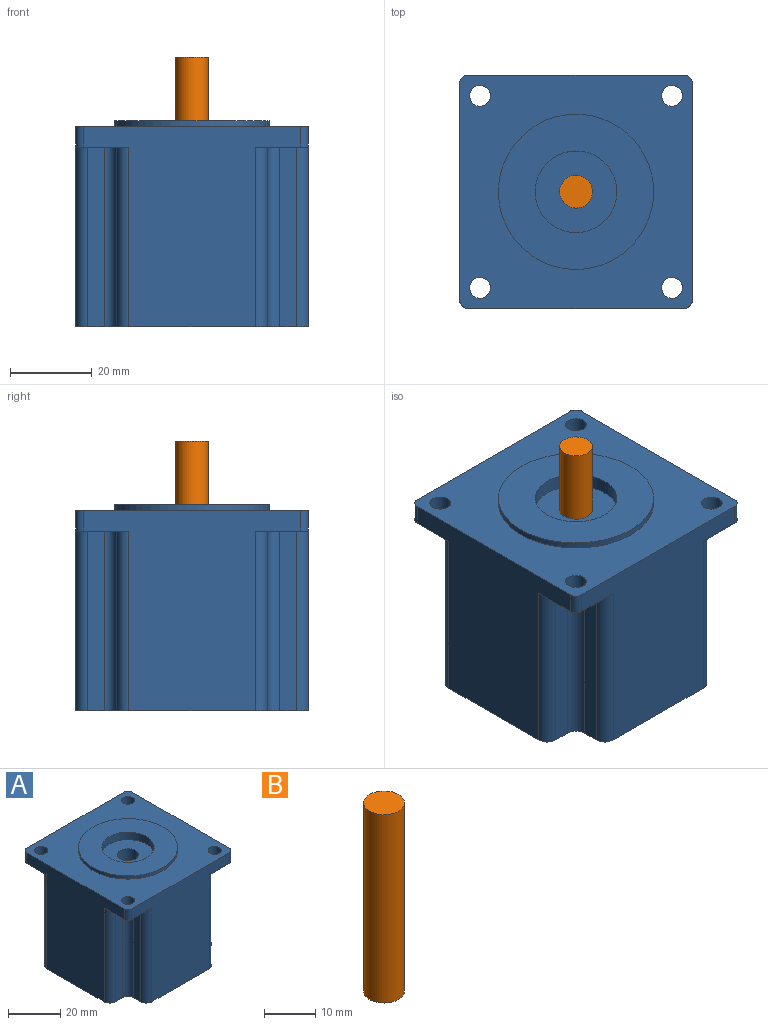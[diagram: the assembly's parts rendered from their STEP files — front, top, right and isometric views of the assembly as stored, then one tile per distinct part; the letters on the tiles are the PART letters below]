
ASSEMBLY  parts=2 mates=1
PART A: 44 faces, bbox 57x57x50.5 mm
  f0: cylinder r=10mm len=20mm, axis (0,0,1), area 219.9mm2, adj f1,f5
  f1: plane 20x20mm, normal (0,0,1), area 263.9mm2, adj f0,f2
  f2: cylinder r=4mm len=25mm, axis (0,0,1), area 628.3mm2, adj f1,f3
  f3: plane 8x8mm, normal (0,0,1), area 50.3mm2, adj f2
  f4: cylinder r=19mm len=38mm, axis (0,0,-1), area 179.1mm2, adj f5,f43
  f5: plane 38x38mm, normal (0,0,1), area 820mm2, adj f0,f4
  f6: plane 44x4mm, normal (-1,0,0), area 176mm2, adj f7,f21,f26,f27
  f7: cylinder r=3mm len=44mm, axis (0,0,1), area 207.3mm2, adj f6,f8,f26,f27
  f8: plane 44x4mm, normal (0,-1,0), area 176mm2, adj f7,f22,f26,f27
  f9: plane 44x4mm, normal (0,1,0), area 176mm2, adj f10,f23,f26,f28
  f10: cylinder r=3mm len=44mm, axis (0,0,1), area 207.3mm2, adj f9,f11,f26,f28
  f11: plane 44x4mm, normal (-1,0,0), area 176mm2, adj f10,f25,f26,f28
  f12: plane 44x4mm, normal (1,0,0), area 176mm2, adj f13,f24,f26,f29
  f13: cylinder r=3mm len=44mm, axis (0,0,1), area 207.3mm2, adj f12,f14,f26,f29
  f14: plane 44x4mm, normal (0,1,0), area 176mm2, adj f13,f18,f26,f29
  f15: plane 44x4mm, normal (0,-1,0), area 176mm2, adj f16,f19,f26,f30
  f16: cylinder r=3mm len=44mm, axis (0,0,1), area 207.3mm2, adj f15,f17,f26,f30
  f17: plane 44x4mm, normal (1,0,0), area 176mm2, adj f16,f20,f26,f30
  f18: cylinder r=3mm len=44mm, axis (0,0,1), area 207.3mm2, adj f14,f26,f29,f32
  f19: cylinder r=3mm len=44mm, axis (0,0,-1), area 207.3mm2, adj f15,f26,f30,f32
  f20: cylinder r=3mm len=44mm, axis (0,0,1), area 207.3mm2, adj f17,f26,f30,f34
  f21: cylinder r=3mm len=44mm, axis (0,0,-1), area 207.3mm2, adj f6,f26,f27,f34
  f22: cylinder r=3mm len=44mm, axis (0,0,-1), area 207.3mm2, adj f8,f26,f27,f36
  f23: cylinder r=3mm len=44mm, axis (0,0,1), area 207.3mm2, adj f9,f26,f28,f36
  f24: cylinder r=3mm len=44mm, axis (0,0,1), area 207.3mm2, adj f12,f26,f29,f38
  f25: cylinder r=3mm len=44mm, axis (0,0,-1), area 207.3mm2, adj f11,f26,f28,f38
  f26: plane 57x57mm, normal (0,0,-1), area 2841.3mm2, adj f6,f7,f8,f9,f10,f11,f12,f13
  f27: plane 13x13mm, normal (0,0,-1), area 80.6mm2, adj f6,f7,f8,f21,f22,f34,f35,f36
  f28: plane 13x13mm, normal (0,0,-1), area 80.6mm2, adj f9,f10,f11,f23,f25,f36,f37,f38
  f29: plane 13x13mm, normal (0,0,-1), area 80.6mm2, adj f12,f13,f14,f18,f24,f31,f32,f38
  f30: plane 13x13mm, normal (0,0,-1), area 80.6mm2, adj f15,f16,f17,f19,f20,f32,f33,f34
  f31: cylinder r=2mm len=5mm, axis (0,0,-1), area 15.7mm2, adj f29,f32,f38,f43
  f32: plane 53x49mm, normal (1,0,0), area 1629mm2, adj f18,f19,f26,f29,f30,f31,f33,f43
  f33: cylinder r=2mm len=5mm, axis (0,0,1), area 15.7mm2, adj f30,f32,f34,f43
  f34: plane 53x49mm, normal (0,-1,0), area 1629mm2, adj f20,f21,f26,f27,f30,f33,f35,f43
  f35: cylinder r=2mm len=5mm, axis (0,0,-1), area 15.7mm2, adj f27,f34,f36,f43
  f36: plane 53x49mm, normal (-1,0,0), area 1629mm2, adj f22,f23,f26,f27,f28,f35,f37,f43
  f37: cylinder r=2mm len=5mm, axis (0,0,1), area 15.7mm2, adj f28,f36,f38,f43
  f38: plane 53x49mm, normal (0,1,0), area 1629mm2, adj f24,f25,f26,f28,f29,f31,f37,f43
  f39: cylinder r=2.55mm len=5.1mm, axis (0,0,-1), area 80.1mm2, adj f27,f43
  f40: cylinder r=2.55mm len=5.1mm, axis (0,0,-1), area 80.1mm2, adj f28,f43
  f41: cylinder r=2.55mm len=5.1mm, axis (0,0,-1), area 80.1mm2, adj f29,f43
  f42: cylinder r=2.55mm len=5.1mm, axis (0,0,-1), area 80.1mm2, adj f30,f43
  f43: plane 57x57mm, normal (0,0,1), area 2029.7mm2, adj f4,f31,f32,f33,f34,f35,f36,f37
PART B: 3 faces, bbox 8x8x45 mm
  f0: cylinder r=4mm len=45mm, axis (0,0,-1), area 1131mm2, adj f1,f2
  f1: plane 8x8mm, normal (0,0,1), area 50.3mm2, adj f0
  f2: plane 8x8mm, normal (0,0,-1), area 50.3mm2, adj f0
PLACE A t=(-2.33,0.89,-52.65)mm
PLACE B t=(-2.33,0.89,-9.15)mm
MATE revolute B.f0 <-> A.f0  axis (0,0,1) through (-2.33,0.89,13.35)mm
